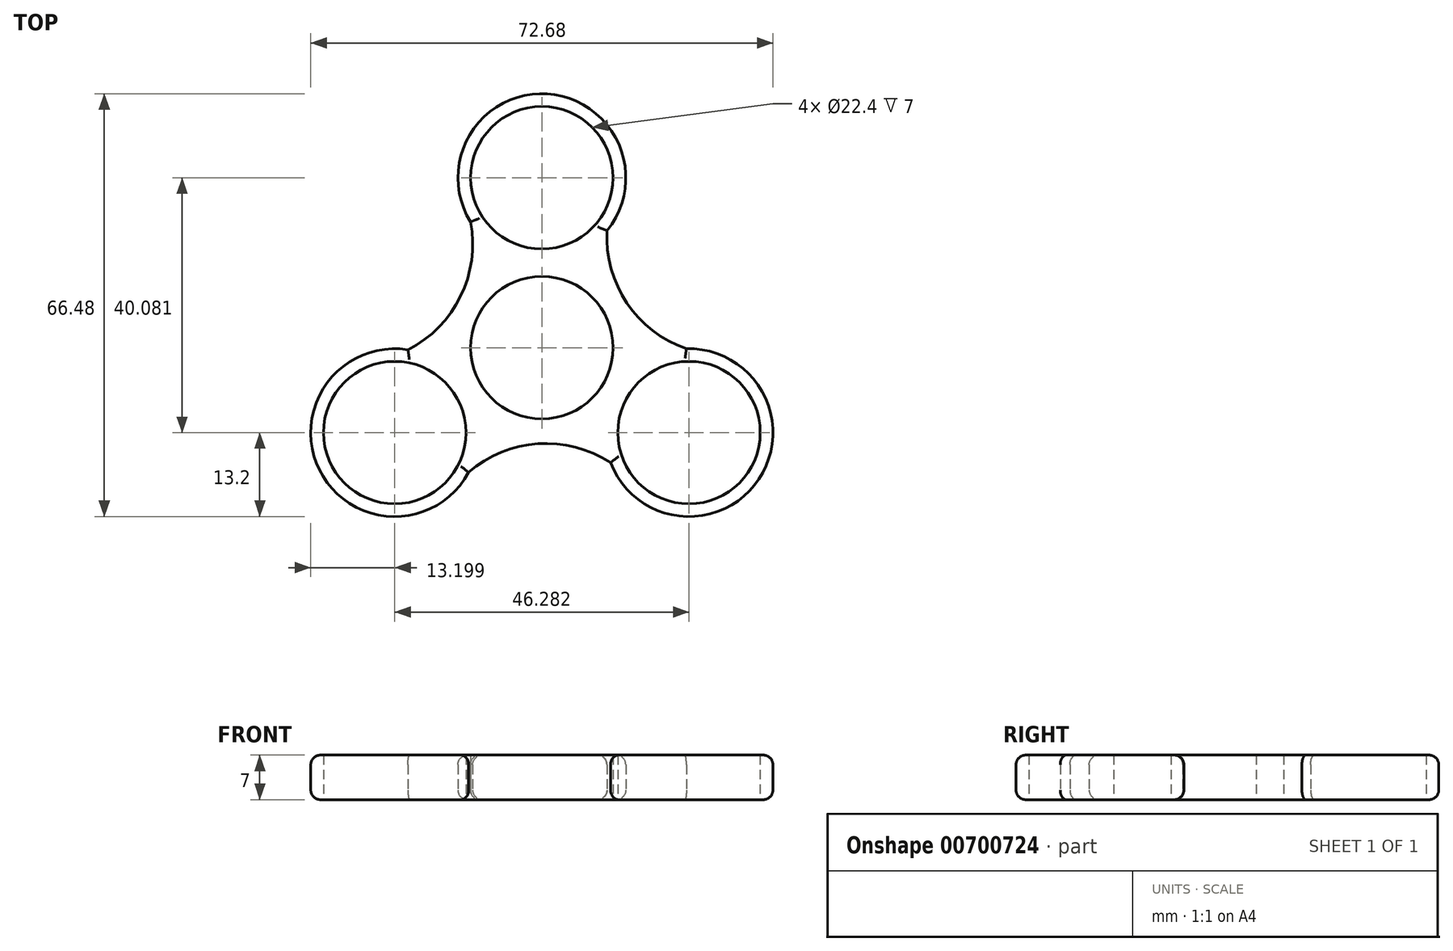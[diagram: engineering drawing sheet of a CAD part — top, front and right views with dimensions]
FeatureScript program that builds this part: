
annotation { "Feature Type Name" : "Feature", "Feature Type Description" : "" }
export const myFeature = defineFeature(function(context is Context, id is Id, definition is map)
    precondition{}
    {
        {
            var Q0;
            Q0=qCreatedBy(makeId("Top.planeOp"),FACE);
            var sketch = newSketch(context, id + "F0", { "sketchPlane" : qUnion([Q0])});
            skCircle(sketch, "E0", {"center": v(0, 0) * mm, "radius": 11.2 * mm});
            skCircle(sketch, "E1", {"center": v(0, 26.72) * mm, "radius": 11.2 * mm});
            skCircle(sketch, "E2", {"center": v(0, 26.72) * mm, "radius": 13.2 * mm});
            skCircle(sketch, "E3.1.0", {"center": v(-23.14, -13.36) * mm, "radius": 13.2 * mm});
            skCircle(sketch, "E3.2.0", {"center": v(23.14, -13.36) * mm, "radius": 13.2 * mm});
            skArc(sketch, "E4", {"start": v(10.25, 18.4) * mm, "mid": v(13.38, 7.03) * mm, "end": v(22.74, -0.17) * mm});
            skArc(sketch, "E5.1.0", {"start": v(-21.06, -0.32) * mm, "mid": v(-12.78, 8.08) * mm, "end": v(-11.22, 19.78) * mm});
            skArc(sketch, "E5.2.0", {"start": v(10.81, -18.08) * mm, "mid": v(-0.6, -15.1) * mm, "end": v(-11.51, -19.6) * mm});
            skCircle(sketch, "E6", {"center": v(-23.14, -13.36) * mm, "radius": 11.2 * mm});
            skCircle(sketch, "E7", {"center": v(23.14, -13.36) * mm, "radius": 11.2 * mm});
            skSolve(sketch);
        }
        {
            var Q0;
            Q0 = qSketchRegion(id + "F0", true);
            extrude(context, id + "F1", {"entities" : qUnion([Q0]), "depth" : 7 * mm, "offsetDistance" : 25 * mm});
        }
        {
            var Q0;
            Q0=makeQuery(id+"F1.opExtrude","CAP_EDGE",EDGE,{"disambiguationData":[OSD([sQuery(id+"F0.wireOp",EDGE,"E3.1.0")])],"isStart":false});
            var Q1;
            Q1=makeQuery(id+"F1.opExtrude","CAP_EDGE",EDGE,{"disambiguationData":[OSD([sQuery(id+"F0.wireOp",EDGE,"E5.1.0")])],"isStart":false});
            var Q2;
            Q2=makeQuery(id+"F1.opExtrude","CAP_EDGE",EDGE,{"disambiguationData":[OSD([sQuery(id+"F0.wireOp",EDGE,"E2")])],"isStart":false});
            var Q3;
            Q3=makeQuery(id+"F1.opExtrude","CAP_EDGE",EDGE,{"disambiguationData":[OSD([sQuery(id+"F0.wireOp",EDGE,"E5.2.0")])],"isStart":false});
            var Q4;
            Q4=makeQuery(id+"F1.opExtrude","CAP_EDGE",EDGE,{"disambiguationData":[OSD([sQuery(id+"F0.wireOp",EDGE,"E3.2.0")])],"isStart":false});
            var Q5;
            Q5=makeQuery(id+"F1.opExtrude","CAP_EDGE",EDGE,{"disambiguationData":[OSD([sQuery(id+"F0.wireOp",EDGE,"E4")])],"isStart":false});
            fillet(context, id + "F2", {"entities" : qUnion([Q0, Q1, Q2, Q3, Q4, Q5]), "radius" : 1.5 * mm, "tangentPropagation" : true, "allowEdgeOverflow" : false});
        }
        {
            var Q0;
            Q0=makeQuery(id+"F1.opExtrude","CAP_EDGE",EDGE,{"disambiguationData":[OSD([sQuery(id+"F0.wireOp",EDGE,"E3.1.0")])],"isStart":true});
            var Q1;
            Q1=makeQuery(id+"F1.opExtrude","CAP_EDGE",EDGE,{"disambiguationData":[OSD([sQuery(id+"F0.wireOp",EDGE,"E5.2.0")])],"isStart":true});
            var Q2;
            Q2=makeQuery(id+"F1.opExtrude","CAP_EDGE",EDGE,{"disambiguationData":[OSD([sQuery(id+"F0.wireOp",EDGE,"E3.2.0")])],"isStart":true});
            var Q3;
            Q3=makeQuery(id+"F1.opExtrude","CAP_EDGE",EDGE,{"disambiguationData":[OSD([sQuery(id+"F0.wireOp",EDGE,"E4")])],"isStart":true});
            var Q4;
            Q4=makeQuery(id+"F1.opExtrude","CAP_EDGE",EDGE,{"disambiguationData":[OSD([sQuery(id+"F0.wireOp",EDGE,"E2")])],"isStart":true});
            var Q5;
            Q5=makeQuery(id+"F1.opExtrude","CAP_EDGE",EDGE,{"disambiguationData":[OSD([sQuery(id+"F0.wireOp",EDGE,"E5.1.0")])],"isStart":true});
            fillet(context, id + "F3", {"entities" : qUnion([Q0, Q1, Q2, Q3, Q4, Q5]), "radius" : 1.5 * mm, "tangentPropagation" : true, "allowEdgeOverflow" : false});
        }
    });
